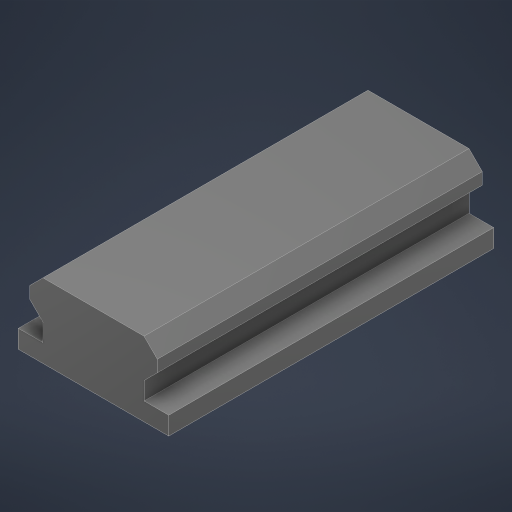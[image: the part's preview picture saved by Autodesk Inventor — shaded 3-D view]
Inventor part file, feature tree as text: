
AUTODESK INVENTOR PART (.ipt)
format: ipt  version: 2023 (Build 270158000, 158)  size: 190,976 bytes
history: native  units: mm
features: extrude x1, mirror x1, sketch x1
ambient origin geometry x8: Origin, YZ Plane, XZ Plane, XY Plane, X Axis, Y Axis, Z Axis, Center Point
bodies: Solid1 (feature_tree)
feature tree (3):
  extrude  "Extrusion1"  TaperAngle=45.0deg  [1 undecoded]
  mirror  "Mirror1"
  sketch  "Sketch1"  dims[d1=21.209mm d5=45.0deg d6=45.0deg d7=4.1656mm d9=18.9992mm d10=9.3218mm d11=25.0mm d12=3.0mm d13=54.0mm d14=0.0mm]
note: 1 required parameter value undecoded (feature->parameter linkage not recoverable at this tier; creation-order binding heuristic only, values carry confidence <= 0.55)
